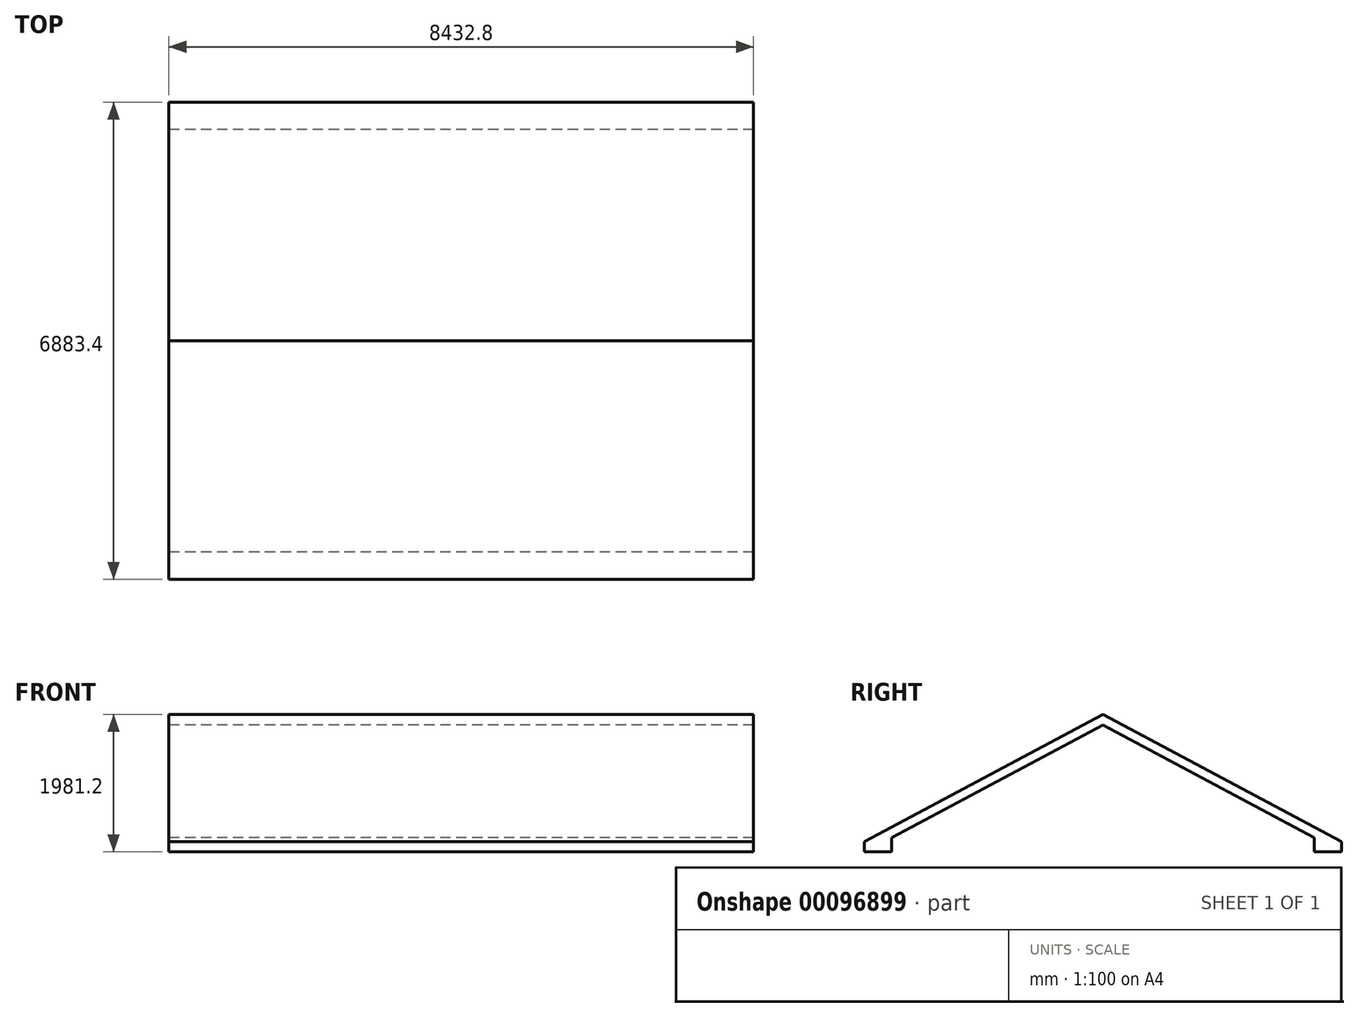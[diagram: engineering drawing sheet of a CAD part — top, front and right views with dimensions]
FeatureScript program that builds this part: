
annotation { "Feature Type Name" : "Feature", "Feature Type Description" : "" }
export const myFeature = defineFeature(function(context is Context, id is Id, definition is map)
    precondition{}
    {
        {
            var Q0;
            Q0=qCreatedBy(makeId("Right.planeOp"),FACE);
            var sketch = newSketch(context, id + "F0", { "sketchPlane" : qUnion([Q0])});
            skLineSegment(sketch, "E0", {"start": v(0, 0) * mm, "end": v(0, 1625.6) * mm, "construction": true});
            skLineSegment(sketch, "E1", {"start": v(-3048, 0) * mm, "end": v(3048, 0) * mm, "construction": true});
            skLineSegment(sketch, "E2", {"start": v(-3048, 0) * mm, "end": v(0, 1625.6) * mm});
            skLineSegment(sketch, "E3", {"start": v(-3048, 0) * mm, "end": v(-3048, -203.2) * mm});
            skLineSegment(sketch, "E4", {"start": v(-3048, -203.2) * mm, "end": v(-3441.7, -203.2) * mm});
            skLineSegment(sketch, "E5", {"start": v(-3441.7, -203.2) * mm, "end": v(-3441.7, -57.57) * mm});
            skLineSegment(sketch, "E6", {"start": v(0, 1778) * mm, "end": v(-3441.7, -57.57) * mm});
            skLineSegment(sketch, "E7.MirrorCS", {"start": v(3048, 0) * mm, "end": v(3048, -203.2) * mm});
            skLineSegment(sketch, "E8.MirrorCS", {"start": v(3441.7, -203.2) * mm, "end": v(3441.7, -57.57) * mm});
            skLineSegment(sketch, "E9.MirrorCS", {"start": v(3048, 0) * mm, "end": v(0, 1625.6) * mm});
            skLineSegment(sketch, "E10.MirrorCS", {"start": v(3048, -203.2) * mm, "end": v(3441.7, -203.2) * mm});
            skLineSegment(sketch, "E11.MirrorCS", {"start": v(0, 1778) * mm, "end": v(3441.7, -57.57) * mm});
            skSolve(sketch);
        }
        {
            var Q0;
            Q0 = qSketchRegion(id + "F0", true);
            extrude(context, id + "F1", {"entities" : qUnion([Q0]), "depth" : 8432.8 * mm});
        }
    });
